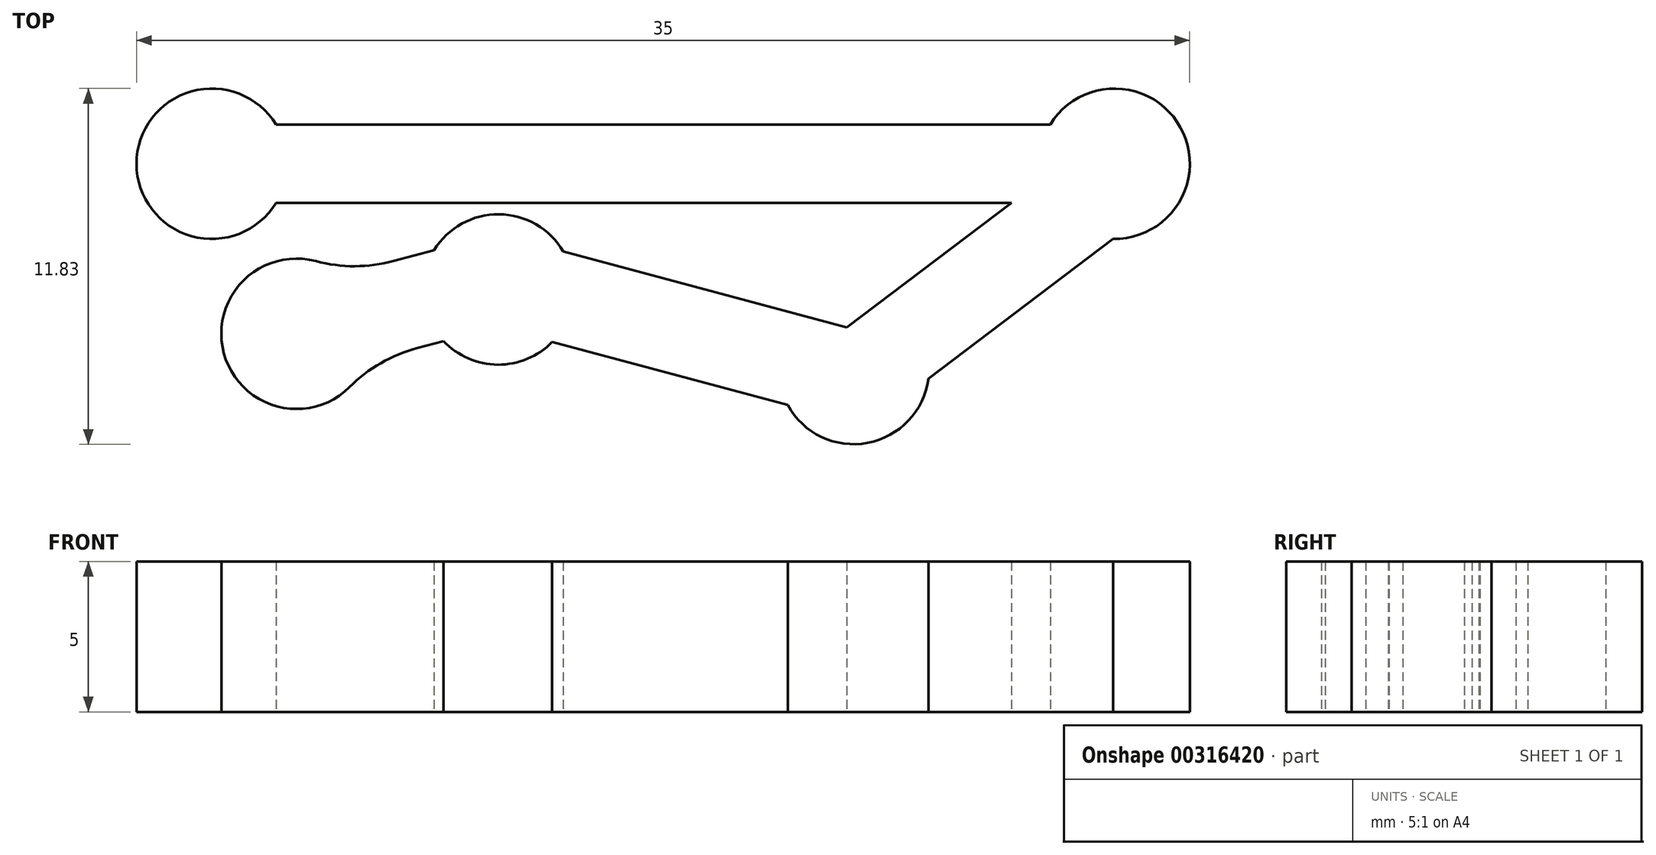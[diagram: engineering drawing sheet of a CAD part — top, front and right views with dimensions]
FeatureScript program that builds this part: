
annotation { "Feature Type Name" : "Feature", "Feature Type Description" : "" }
export const myFeature = defineFeature(function(context is Context, id is Id, definition is map)
    precondition{}
    {
        {
            var Q0;
            Q0=qCreatedBy(makeId("Top.planeOp"),FACE);
            var sketch = newSketch(context, id + "F0", { "sketchPlane" : qUnion([Q0])});
            skCircle(sketch, "E0", {"center": v(1.74, -0.42) * mm, "radius": 2.5 * mm});
            skLineSegment(sketch, "E1.bottom", {"start": v(1.74, 0.88) * mm, "end": v(31.74, 0.88) * mm});
            skLineSegment(sketch, "E1.top", {"start": v(1.74, -1.72) * mm, "end": v(31.74, -1.72) * mm});
            skLineSegment(sketch, "E1.left", {"start": v(1.74, 0.88) * mm, "end": v(1.74, -1.72) * mm});
            skLineSegment(sketch, "E1.right", {"start": v(31.74, 0.88) * mm, "end": v(31.74, -1.72) * mm});
            skCircle(sketch, "E2", {"center": v(31.74, -0.42) * mm, "radius": 2.5 * mm});
            skLineSegment(sketch, "E3.bottom", {"start": v(21.67, -6.75) * mm, "end": v(31.74, 0.88) * mm});
            skLineSegment(sketch, "E3.top", {"start": v(23.48, -9.14) * mm, "end": v(33.55, -1.51) * mm});
            skLineSegment(sketch, "E3.left", {"start": v(21.67, -6.75) * mm, "end": v(23.48, -9.14) * mm});
            skLineSegment(sketch, "E3.right", {"start": v(31.74, 0.88) * mm, "end": v(33.55, -1.51) * mm});
            skCircle(sketch, "E4", {"center": v(23.07, -7.25) * mm, "radius": 2.5 * mm});
            skLineSegment(sketch, "E5.bottom", {"start": v(24.26, -6.25) * mm, "end": v(11.2, -2.75) * mm});
            skLineSegment(sketch, "E5.top", {"start": v(23.48, -9.14) * mm, "end": v(10.42, -5.65) * mm});
            skLineSegment(sketch, "E5.left", {"start": v(24.26, -6.25) * mm, "end": v(23.48, -9.14) * mm});
            skLineSegment(sketch, "E5.right", {"start": v(11.2, -2.75) * mm, "end": v(10.42, -5.65) * mm});
            skLineSegment(sketch, "E6.bottom", {"start": v(4.17, -4.63) * mm, "end": v(11.4, -2.7) * mm});
            skLineSegment(sketch, "E6.top", {"start": v(4.95, -7.53) * mm, "end": v(12.17, -5.6) * mm});
            skLineSegment(sketch, "E6.left", {"start": v(4.17, -4.63) * mm, "end": v(4.95, -7.53) * mm});
            skLineSegment(sketch, "E6.right", {"start": v(11.4, -2.7) * mm, "end": v(12.17, -5.6) * mm});
            skCircle(sketch, "E7", {"center": v(11.26, -4.6) * mm, "radius": 2.5 * mm});
            skCircle(sketch, "E8", {"center": v(4.56, -6.08) * mm, "radius": 2.5 * mm});
            skSolve(sketch);
        }
        {
            var Q0;
            {var subQ0=sQuery(id+"F0.wireOp",EDGE,"E1.bottom");var subQ1=sQuery(id+"F0.wireOp",EDGE,"E0");var subQ2=makeQuery(id+"F0.imprint","INTERSECT",VERTEX,{"derivedFrom":[subQ1,subQ0]});Q0=makeQuery(id+"F0.imprint","IMPRINT",FACE,{"disambiguationData":[TD([[makeQuery(id+"F0.imprint","IMPRINT",EDGE,{"disambiguationData":[TD([[subQ2,1.0]])],"derivedFrom":subQ1}),-1.0]])]});}
            var Q1;
            {var subQ0=sQuery(id+"F0.wireOp",EDGE,"E3.right");Q1=makeQuery(id+"F0.imprint","IMPRINT",FACE,{"disambiguationData":[TD([[makeQuery(id+"F0.imprint","IMPRINT",EDGE,{"derivedFrom":subQ0}),1.0]])]});}
            var Q2;
            {var subQ4=sQuery(id+"F0.wireOp",EDGE,"E1.right");Q2=makeQuery(id+"F0.imprint","IMPRINT",FACE,{"disambiguationData":[TD([[makeQuery(id+"F0.imprint","IMPRINT",EDGE,{"derivedFrom":subQ4}),1.0]])]});}
            var Q3;
            {var subQ1=sQuery(id+"F0.wireOp",EDGE,"E1.bottom");var subQ3=sQuery(id+"F0.wireOp",EDGE,"E2");var subQ4=makeQuery(id+"F0.imprint","INTERSECT",VERTEX,{"derivedFrom":[subQ1,subQ3]});Q3=makeQuery(id+"F0.imprint","IMPRINT",FACE,{"disambiguationData":[TD([[makeQuery(id+"F0.imprint","IMPRINT",EDGE,{"disambiguationData":[TD([[subQ4,-1.0]])],"derivedFrom":subQ3}),1.0]])]});}
            var Q4;
            {var subQ0=sQuery(id+"F0.wireOp",EDGE,"E1.right");Q4=makeQuery(id+"F0.imprint","IMPRINT",FACE,{"disambiguationData":[TD([[makeQuery(id+"F0.imprint","IMPRINT",EDGE,{"derivedFrom":subQ0}),-1.0]])]});}
            var Q5;
            {var subQ5=sQuery(id+"F0.wireOp",EDGE,"E1.top");var subQ7=sQuery(id+"F0.wireOp",EDGE,"E3.bottom");var subQ8=makeQuery(id+"F0.imprint","INTERSECT",VERTEX,{"derivedFrom":[subQ5,subQ7]});Q5=makeQuery(id+"F0.imprint","IMPRINT",FACE,{"disambiguationData":[TD([[makeQuery(id+"F0.imprint","IMPRINT",EDGE,{"disambiguationData":[TD([[subQ8,-1.0]])],"derivedFrom":subQ5}),-1.0]])]});}
            var Q6;
            {var subQ0=sQuery(id+"F0.wireOp",EDGE,"E3.bottom");var subQ1=sQuery(id+"F0.wireOp",EDGE,"E1.top");var subQ2=makeQuery(id+"F0.imprint","INTERSECT",VERTEX,{"derivedFrom":[subQ1,subQ0]});Q6=makeQuery(id+"F0.imprint","IMPRINT",FACE,{"disambiguationData":[TD([[makeQuery(id+"F0.imprint","IMPRINT",EDGE,{"disambiguationData":[TD([[subQ2,-1.0]])],"derivedFrom":subQ1}),1.0]])]});}
            var Q7;
            {var subQ0=sQuery(id+"F0.wireOp",EDGE,"E5.left");Q7=makeQuery(id+"F0.imprint","IMPRINT",FACE,{"disambiguationData":[TD([[makeQuery(id+"F0.imprint","IMPRINT",EDGE,{"derivedFrom":subQ0}),1.0]])]});}
            var Q8;
            {var subQ1=sQuery(id+"F0.wireOp",EDGE,"E3.top");var subQ3=sQuery(id+"F0.wireOp",EDGE,"E4");var subQ4=makeQuery(id+"F0.imprint","INTERSECT",VERTEX,{"derivedFrom":[subQ1,subQ3]});Q8=makeQuery(id+"F0.imprint","IMPRINT",FACE,{"disambiguationData":[TD([[makeQuery(id+"F0.imprint","IMPRINT",EDGE,{"disambiguationData":[TD([[subQ4,1.0]])],"derivedFrom":subQ3}),1.0]])]});}
            var Q9;
            {var subQ5=sQuery(id+"F0.wireOp",EDGE,"E3.left");Q9=makeQuery(id+"F0.imprint","IMPRINT",FACE,{"disambiguationData":[TD([[makeQuery(id+"F0.imprint","IMPRINT",EDGE,{"derivedFrom":subQ5}),-1.0]])]});}
            var Q10;
            {var subQ0=sQuery(id+"F0.wireOp",EDGE,"E3.left");Q10=makeQuery(id+"F0.imprint","IMPRINT",FACE,{"disambiguationData":[TD([[makeQuery(id+"F0.imprint","IMPRINT",EDGE,{"derivedFrom":subQ0}),1.0]])]});}
            var Q11;
            {var subQ0=sQuery(id+"F0.wireOp",EDGE,"E5.bottom");var subQ1=sQuery(id+"F0.wireOp",EDGE,"E4");var subQ2=makeQuery(id+"F0.imprint","INTERSECT",VERTEX,{"derivedFrom":[subQ1,subQ0]});Q11=makeQuery(id+"F0.imprint","IMPRINT",FACE,{"disambiguationData":[TD([[makeQuery(id+"F0.imprint","IMPRINT",EDGE,{"disambiguationData":[TD([[subQ2,-1.0]])],"derivedFrom":subQ1}),-1.0]])]});}
            var Q12;
            {var subQ3=sQuery(id+"F0.wireOp",EDGE,"E5.bottom");var subQ7=sQuery(id+"F0.wireOp",EDGE,"E7");var subQ9=makeQuery(id+"F0.imprint","INTERSECT",VERTEX,{"derivedFrom":[subQ3,subQ7]});Q12=makeQuery(id+"F0.imprint","IMPRINT",FACE,{"disambiguationData":[TD([[makeQuery(id+"F0.imprint","IMPRINT",EDGE,{"disambiguationData":[TD([[subQ9,-1.0]])],"derivedFrom":subQ3}),1.0]])]});}
            var Q13;
            {var subQ0=sQuery(id+"F0.wireOp",EDGE,"E7");var subQ1=sQuery(id+"F0.wireOp",EDGE,"E5.bottom");var subQ2=makeQuery(id+"F0.imprint","INTERSECT",VERTEX,{"derivedFrom":[subQ1,subQ0]});Q13=makeQuery(id+"F0.imprint","IMPRINT",FACE,{"disambiguationData":[TD([[makeQuery(id+"F0.imprint","IMPRINT",EDGE,{"disambiguationData":[TD([[subQ2,-1.0]])],"derivedFrom":subQ1}),-1.0]])]});}
            var Q14;
            {var subQ0=sQuery(id+"F0.wireOp",EDGE,"E5.right");Q14=makeQuery(id+"F0.imprint","IMPRINT",FACE,{"disambiguationData":[TD([[makeQuery(id+"F0.imprint","IMPRINT",EDGE,{"derivedFrom":subQ0}),-1.0]])]});}
            var Q15;
            {var subQ5=sQuery(id+"F0.wireOp",EDGE,"E5.right");Q15=makeQuery(id+"F0.imprint","IMPRINT",FACE,{"disambiguationData":[TD([[makeQuery(id+"F0.imprint","IMPRINT",EDGE,{"derivedFrom":subQ5}),1.0]])]});}
            var Q16;
            {var subQ0=sQuery(id+"F0.wireOp",EDGE,"E7");var subQ1=sQuery(id+"F0.wireOp",EDGE,"E5.top");var subQ2=makeQuery(id+"F0.imprint","INTERSECT",VERTEX,{"derivedFrom":[subQ1,subQ0]});Q16=makeQuery(id+"F0.imprint","IMPRINT",FACE,{"disambiguationData":[TD([[makeQuery(id+"F0.imprint","IMPRINT",EDGE,{"disambiguationData":[TD([[subQ2,-1.0]])],"derivedFrom":subQ1}),1.0]])]});}
            var Q17;
            {var subQ0=sQuery(id+"F0.wireOp",EDGE,"E8");var subQ1=sQuery(id+"F0.wireOp",EDGE,"E6.bottom");var subQ2=makeQuery(id+"F0.imprint","INTERSECT",VERTEX,{"derivedFrom":[subQ1,subQ0]});Q17=makeQuery(id+"F0.imprint","IMPRINT",FACE,{"disambiguationData":[TD([[makeQuery(id+"F0.imprint","IMPRINT",EDGE,{"disambiguationData":[TD([[subQ2,-1.0]])],"derivedFrom":subQ1}),-1.0]])]});}
            var Q18;
            {var subQ0=sQuery(id+"F0.wireOp",EDGE,"E6.left");Q18=makeQuery(id+"F0.imprint","IMPRINT",FACE,{"disambiguationData":[TD([[makeQuery(id+"F0.imprint","IMPRINT",EDGE,{"derivedFrom":subQ0}),-1.0]])]});}
            var Q19;
            {var subQ0=sQuery(id+"F0.wireOp",EDGE,"E6.left");Q19=makeQuery(id+"F0.imprint","IMPRINT",FACE,{"disambiguationData":[TD([[makeQuery(id+"F0.imprint","IMPRINT",EDGE,{"derivedFrom":subQ0}),1.0]])]});}
            var Q20;
            Q20=sQuery(id+"F0.wireOp",EDGE,"E5.top");
            var Q21;
            Q21=sQuery(id+"F0.wireOp",EDGE,"E6.top");
            var Q22;
            Q22=sQuery(id+"F0.wireOp",EDGE,"E2");
            var Q23;
            Q23=sQuery(id+"F0.wireOp",EDGE,"E3.bottom");
            var Q24;
            Q24=sQuery(id+"F0.wireOp",EDGE,"E1.right");
            var Q25;
            Q25=sQuery(id+"F0.wireOp",EDGE,"E1.top");
            var Q26;
            Q26=sQuery(id+"F0.wireOp",EDGE,"E1.left");
            var Q27;
            Q27=sQuery(id+"F0.wireOp",EDGE,"E6.bottom");
            var Q28;
            Q28=sQuery(id+"F0.wireOp",EDGE,"E3.top");
            var Q29;
            Q29=sQuery(id+"F0.wireOp",EDGE,"E0");
            var Q30;
            Q30=sQuery(id+"F0.wireOp",EDGE,"E4");
            var Q31;
            Q31=sQuery(id+"F0.wireOp",EDGE,"E3.left");
            var Q32;
            Q32=sQuery(id+"F0.wireOp",EDGE,"E5.bottom");
            var Q33;
            Q33=sQuery(id+"F0.wireOp",EDGE,"E6.right");
            var Q34;
            Q34=sQuery(id+"F0.wireOp",EDGE,"E5.right");
            var Q35;
            Q35=sQuery(id+"F0.wireOp",EDGE,"E8");
            var Q36;
            Q36=sQuery(id+"F0.wireOp",EDGE,"E7");
            var Q37;
            Q37=sQuery(id+"F0.wireOp",EDGE,"E1.bottom");
            var Q38;
            Q38=sQuery(id+"F0.wireOp",EDGE,"E6.left");
            var Q39;
            Q39=sQuery(id+"F0.wireOp",EDGE,"E5.left");
            var Q40;
            Q40=sQuery(id+"F0.wireOp",EDGE,"E3.right");
            extrude(context, id + "F1", {"entities" : qUnion([Q0, Q1, Q2, Q3, Q4, Q5, Q6, Q7, Q8, Q9, Q10, Q11, Q12, Q13, Q14, Q15, Q16, Q17, Q18, Q19]), "surfaceEntities" : qUnion([Q20, Q21, Q22, Q23, Q24, Q25, Q26, Q27, Q28, Q29, Q30, Q31, Q32, Q33, Q34, Q35, Q36, Q37, Q38, Q39, Q40]), "depth" : 5 * mm});
        }
        {
            var Q0;
            {var subQ5=sQuery(id+"F0.wireOp",EDGE,"E1.left");Q0=makeQuery(id+"F0.imprint","IMPRINT",FACE,{"disambiguationData":[TD([[makeQuery(id+"F0.imprint","IMPRINT",EDGE,{"derivedFrom":subQ5}),-1.0]])]});}
            var Q1;
            {var subQ5=sQuery(id+"F0.wireOp",EDGE,"E1.left");Q1=makeQuery(id+"F0.imprint","IMPRINT",FACE,{"disambiguationData":[TD([[makeQuery(id+"F0.imprint","IMPRINT",EDGE,{"derivedFrom":subQ5}),1.0]])]});}
            extrude(context, id + "F2", {"entities" : qUnion([Q0, Q1]), "operationType" : NewBodyOperationType.ADD, "depth" : 5 * mm});
        }
        {
            var Q0;
            Q0=makeQuery(id+"F1.opExtrude","SWEPT_EDGE",EDGE,{"disambiguationData":[OSD([sQuery(id+"F0.wireOp",EDGE,"E0"),sQuery(id+"F0.wireOp",EDGE,"E1.bottom")])]});
            var Q1;
            Q1=makeQuery(id+"F1.opExtrude","SWEPT_EDGE",EDGE,{"disambiguationData":[OSD([sQuery(id+"F0.wireOp",EDGE,"E0"),sQuery(id+"F0.wireOp",EDGE,"E1.top")])]});
            var Q2;
            Q2=makeQuery(id+"F1.opExtrude","SWEPT_EDGE",EDGE,{"disambiguationData":[OSD([sQuery(id+"F0.wireOp",EDGE,"E6.top"),sQuery(id+"F0.wireOp",EDGE,"E8")])]});
            var Q3;
            Q3=makeQuery(id+"F1.opExtrude","SWEPT_EDGE",EDGE,{"disambiguationData":[OSD([sQuery(id+"F0.wireOp",EDGE,"E6.bottom"),sQuery(id+"F0.wireOp",EDGE,"E8")])]});
            fillet(context, id + "F3", {"entities" : qUnion([Q0, Q1, Q2, Q3]), "radius" : 5 * mm, "tangentPropagation" : true, "allowEdgeOverflow" : false});
        }
    });
